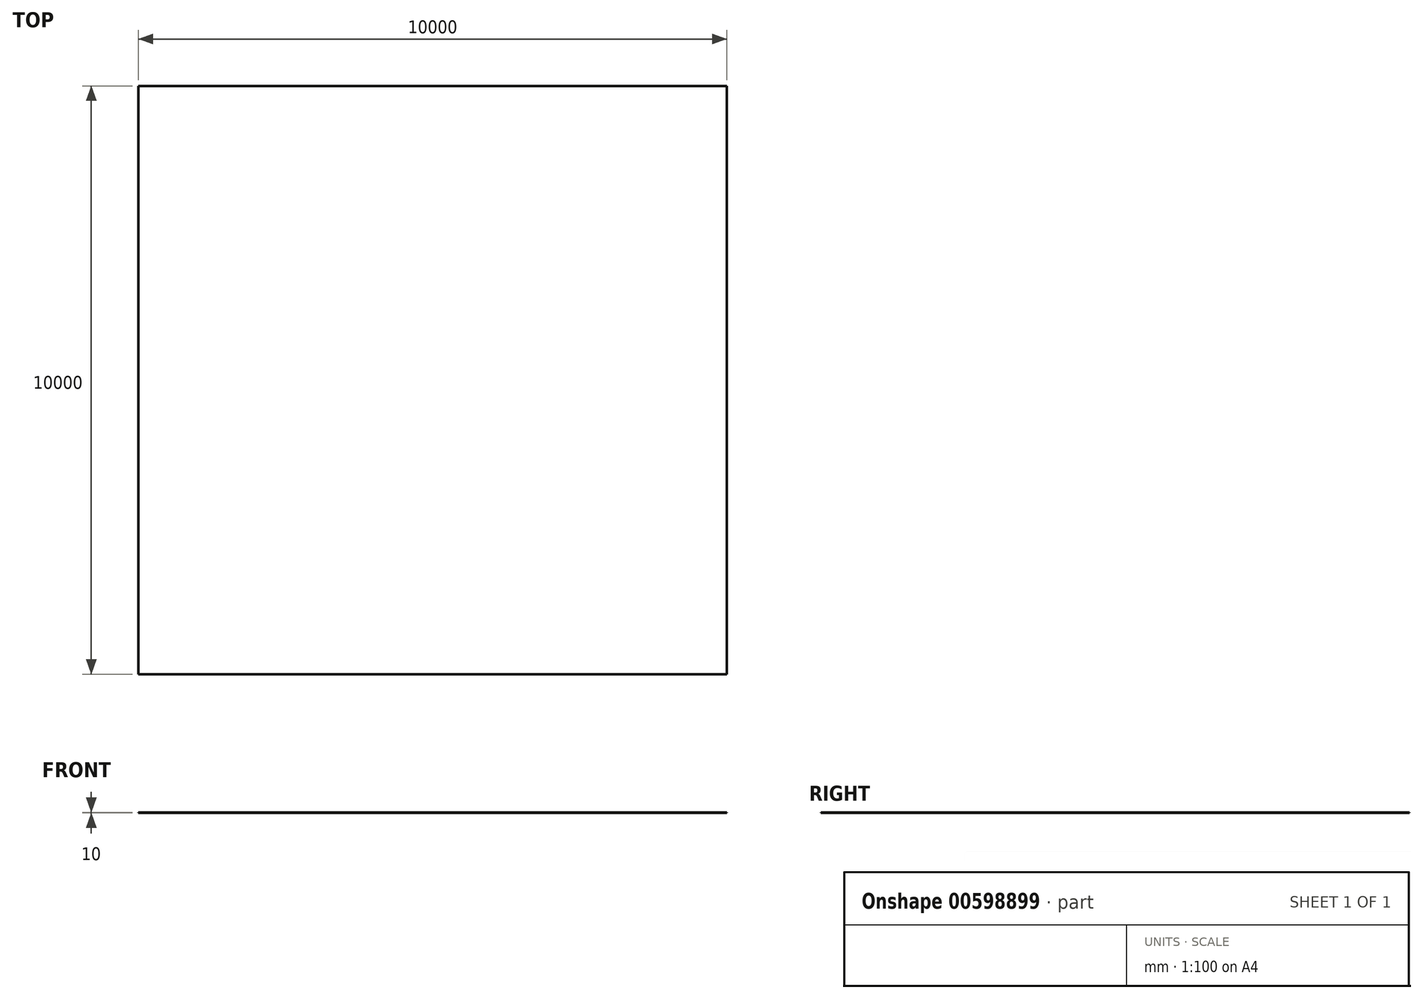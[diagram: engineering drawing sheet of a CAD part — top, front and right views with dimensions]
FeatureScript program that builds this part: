
annotation { "Feature Type Name" : "Feature", "Feature Type Description" : "" }
export const myFeature = defineFeature(function(context is Context, id is Id, definition is map)
    precondition{}
    {
        {
            var Q0;
            Q0=qCreatedBy(makeId("Top.planeOp"),FACE);
            var sketch = newSketch(context, id + "F0", { "sketchPlane" : qUnion([Q0])});
            skLineSegment(sketch, "E0.bottom", {"start": v(5000, -5000) * mm, "end": v(-5000, -5000) * mm});
            skLineSegment(sketch, "E0.top", {"start": v(5000, 5000) * mm, "end": v(-5000, 5000) * mm});
            skLineSegment(sketch, "E0.left", {"start": v(5000, -5000) * mm, "end": v(5000, 5000) * mm});
            skLineSegment(sketch, "E0.right", {"start": v(-5000, -5000) * mm, "end": v(-5000, 5000) * mm});
            skPoint(sketch, "E0.middle", {"position": v(0, 0) * mm});
            skSolve(sketch);
        }
        {
            var Q0;
            Q0 = qSketchRegion(id + "F0", true);
            extrude(context, id + "F1", {"entities" : qUnion([Q0]), "depth" : 10 * mm, "offsetDistance" : 25 * mm});
        }
    });
